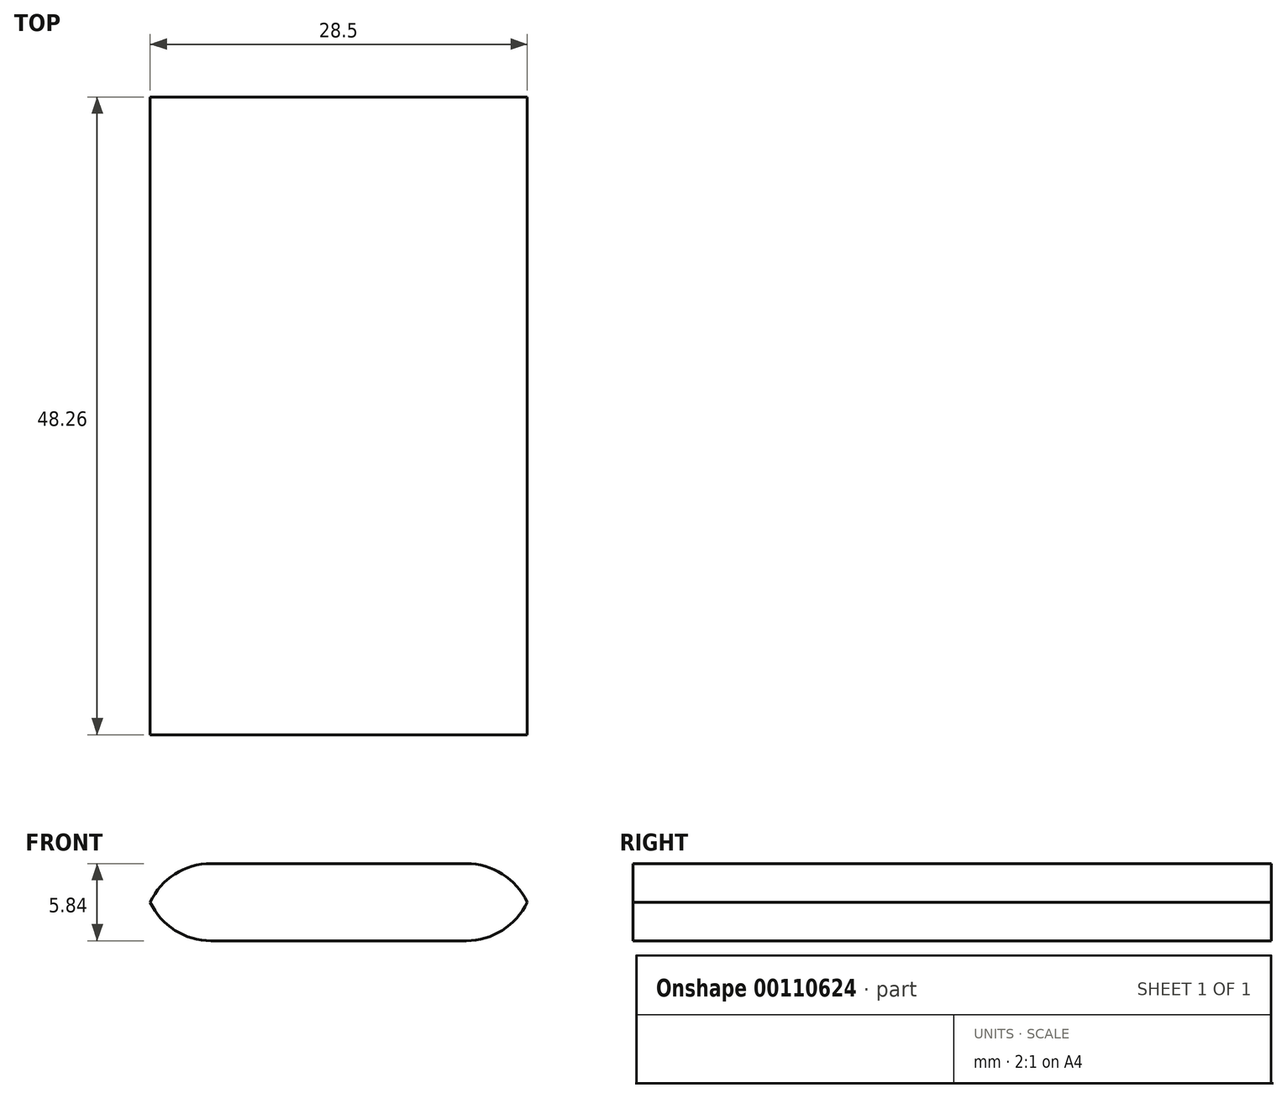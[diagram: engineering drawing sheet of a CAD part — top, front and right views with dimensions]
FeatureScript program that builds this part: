
annotation { "Feature Type Name" : "Feature", "Feature Type Description" : "" }
export const myFeature = defineFeature(function(context is Context, id is Id, definition is map)
    precondition{}
    {
        {
            var Q0;
            Q0=qCreatedBy(makeId("Top.planeOp"),FACE);
            var sketch = newSketch(context, id + "F0", { "sketchPlane" : qUnion([Q0])});
            skLineSegment(sketch, "E0.rect.bottom", {"start": v(14.73, 24.13) * mm, "end": v(-14.73, 24.13) * mm});
            skLineSegment(sketch, "E0.rect.top", {"start": v(14.73, -24.13) * mm, "end": v(-14.73, -24.13) * mm});
            skLineSegment(sketch, "E0.rect.left", {"start": v(14.73, 24.13) * mm, "end": v(14.73, -24.13) * mm});
            skLineSegment(sketch, "E0.rect.right", {"start": v(-14.73, 24.13) * mm, "end": v(-14.73, -24.13) * mm});
            skPoint(sketch, "E0.rect.middle", {"position": v(0, 0) * mm});
            skSolve(sketch);
        }
        {
            var Q0;
            Q0=qSketchRegion(id+"F0",true);
            extrude(context, id + "F1", {"entities" : qUnion([Q0]), "depth" : 5.84 * mm});
        }
        {
            var Q0;
            Q0=makeQuery(id+"F1.opExtrude","CAP_EDGE",EDGE,{"disambiguationData":[OSD([sQuery(id+"F0.wireOp",EDGE,"E0.rect.right")])],"isStart":false});
            var Q1;
            Q1=makeQuery(id+"F1.opExtrude","CAP_EDGE",EDGE,{"disambiguationData":[OSD([sQuery(id+"F0.wireOp",EDGE,"E0.rect.left")])],"isStart":false});
            var Q2;
            Q2=makeQuery(id+"F1.opExtrude","CAP_EDGE",EDGE,{"disambiguationData":[OSD([sQuery(id+"F0.wireOp",EDGE,"E0.rect.left")])],"isStart":true});
            var Q3;
            Q3=makeQuery(id+"F1.opExtrude","CAP_EDGE",EDGE,{"disambiguationData":[OSD([sQuery(id+"F0.wireOp",EDGE,"E0.rect.right")])],"isStart":true});
            fillet(context, id + "F2", {"entities" : qUnion([Q0, Q1, Q2, Q3]), "radius" : 5.08 * mm, "tangentPropagation" : true, "allowEdgeOverflow" : false});
        }
    });
